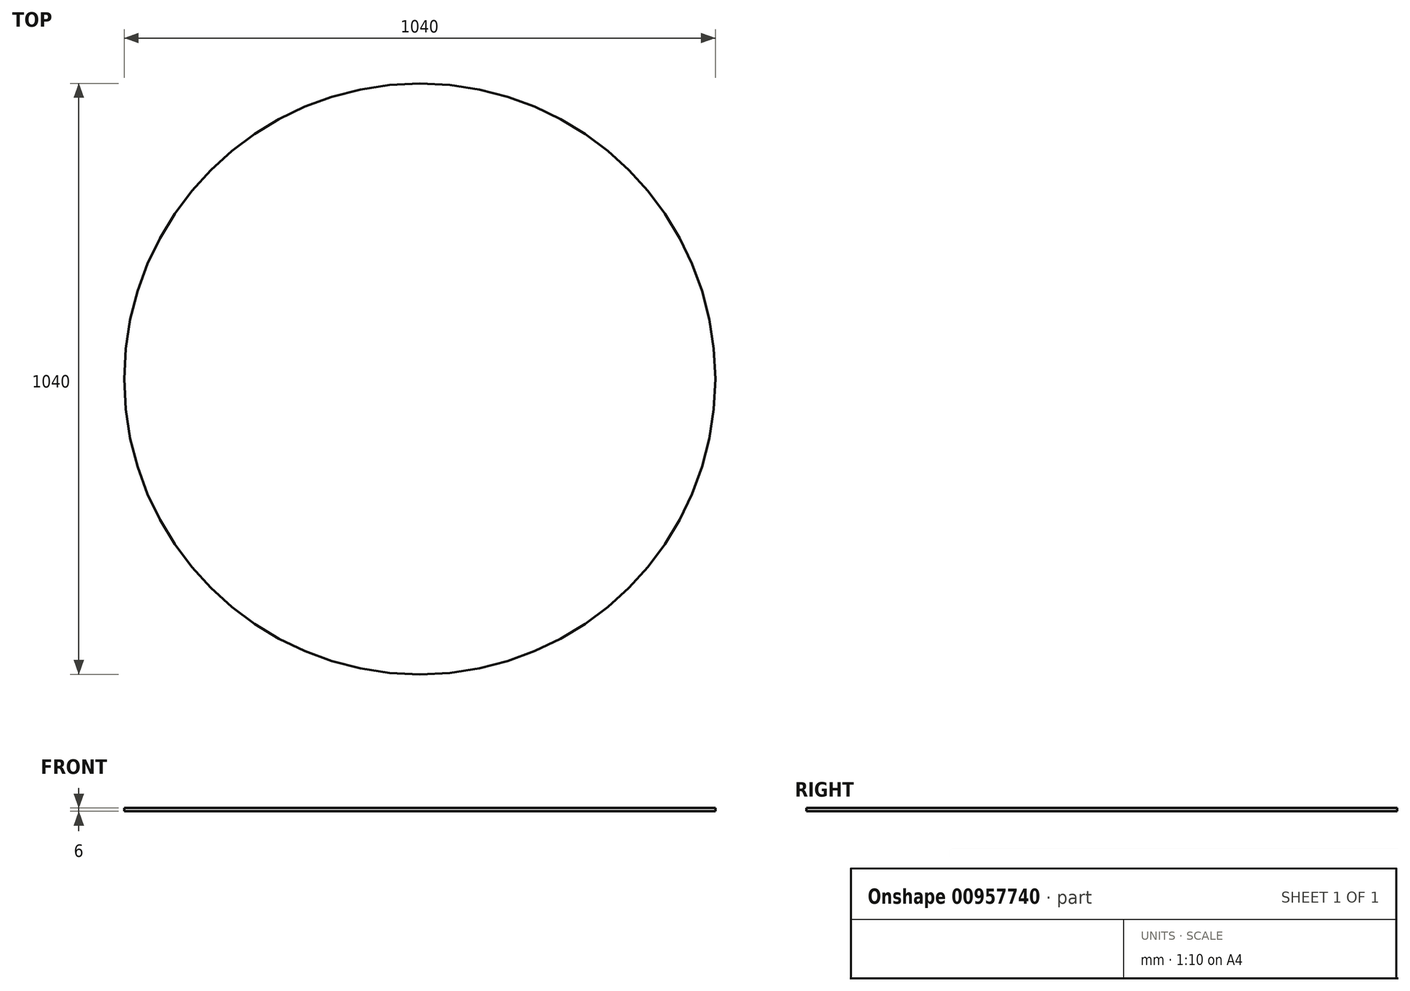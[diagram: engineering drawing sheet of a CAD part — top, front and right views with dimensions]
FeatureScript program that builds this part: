
annotation { "Feature Type Name" : "Feature", "Feature Type Description" : "" }
export const myFeature = defineFeature(function(context is Context, id is Id, definition is map)
    precondition{}
    {
        {
            var Q0;
            Q0=qCreatedBy(makeId("Front.planeOp"),FACE);
            var sketch = newSketch(context, id + "F0", { "sketchPlane" : qUnion([Q0])});
            skLineSegment(sketch, "E0.bottom", {"start": v(-520, 6) * mm, "end": v(0, 6) * mm});
            skLineSegment(sketch, "E0.top", {"start": v(-520, 0) * mm, "end": v(0, 0) * mm});
            skLineSegment(sketch, "E0.left", {"start": v(-520, 6) * mm, "end": v(-520, 0) * mm});
            skLineSegment(sketch, "E0.right", {"start": v(0, 6) * mm, "end": v(0, 0) * mm});
            skSolve(sketch);
        }
        {
            var Q0;
            Q0=qCreatedBy(makeId("Front.planeOp"),FACE);
            var sketch = newSketch(context, id + "F1", { "sketchPlane" : qUnion([Q0])});
            skLineSegment(sketch, "E1", {"start": v(0, 0) * mm, "end": v(0, 102.24) * mm, "construction": true});
            skSolve(sketch);
        }
        {
            var Q0;
            Q0=qSketchRegion(id+"F0",true);
            var Q1;
            Q1=sQuery(id+"F1.wireOp",EDGE,"E1");
            revolve(context, id + "F2", {"surfaceOperationType" : NewSurfaceOperationType.NEW, "entities" : qUnion([Q0]), "axis" : qUnion([Q1]), "revolveType" : RevolveType.FULL, "oppositeDirection" : true});
        }
    });
